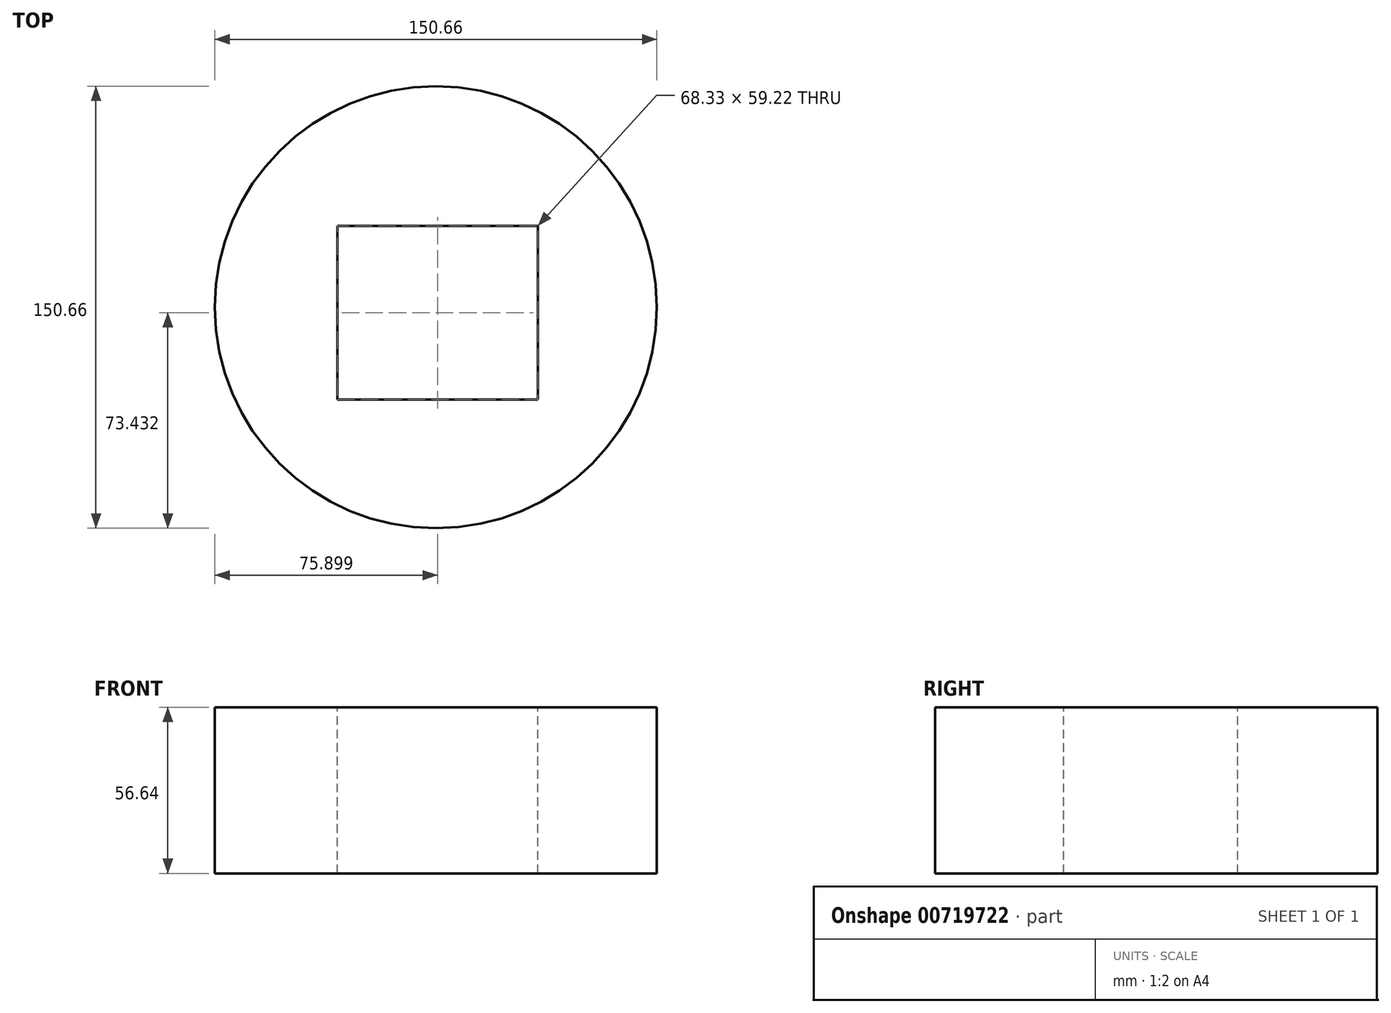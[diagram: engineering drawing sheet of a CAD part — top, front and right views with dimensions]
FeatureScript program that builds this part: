
annotation { "Feature Type Name" : "Feature", "Feature Type Description" : "" }
export const myFeature = defineFeature(function(context is Context, id is Id, definition is map)
    precondition{}
    {
        {
            var Q0;
            Q0=qCreatedBy(makeId("Top.planeOp"),FACE);
            var sketch = newSketch(context, id + "F0", { "sketchPlane" : qUnion([Q0])});
            skCircle(sketch, "E0", {"center": v(0, 0) * mm, "radius": 75.33 * mm});
            skSolve(sketch);
        }
        {
            var Q0;
            Q0=makeQuery(id+"F0.imprint","IMPRINT",FACE,{"disambiguationData":[TD([[makeQuery(id+"F0.imprint","IMPRINT",EDGE,{"derivedFrom":sQuery(id+"F0.wireOp",EDGE,"E0")}),1.0]])]});
            extrude(context, id + "F1", {"entities" : qUnion([Q0]), "depth" : 56.64 * mm, "offsetDistance" : 25.4 * mm});
        }
        {
            var Q0;
            Q0=makeQuery(id+"F1.opExtrude","CAP_FACE",FACE,{"disambiguationData":[OSD([sQuery(id+"F0.wireOp",EDGE,"E0")])],"isStart":false});
            var sketch = newSketch(context, id + "F2", { "sketchPlane" : qUnion([Q0])});
            skLineSegment(sketch, "E1.bottom", {"start": v(-33.6, 27.71) * mm, "end": v(34.73, 27.71) * mm});
            skLineSegment(sketch, "E1.top", {"start": v(-33.6, -31.5) * mm, "end": v(34.73, -31.5) * mm});
            skLineSegment(sketch, "E1.left", {"start": v(-33.6, 27.71) * mm, "end": v(-33.6, -31.5) * mm});
            skLineSegment(sketch, "E1.right", {"start": v(34.73, 27.71) * mm, "end": v(34.73, -31.5) * mm});
            skSolve(sketch);
        }
        {
            var Q0;
            Q0=makeQuery(id+"F2.imprint","IMPRINT",FACE,{"disambiguationData":[TD([[makeQuery(id+"F2.imprint","IMPRINT",EDGE,{"derivedFrom":sQuery(id+"F2.wireOp",EDGE,"E1.bottom")}),-1.0]])]});
            extrude(context, id + "F3", {"entities" : qUnion([Q0]), "operationType" : NewBodyOperationType.REMOVE, "oppositeDirection" : true, "depth" : 82.04 * mm, "offsetDistance" : 25.4 * mm});
        }
    });
